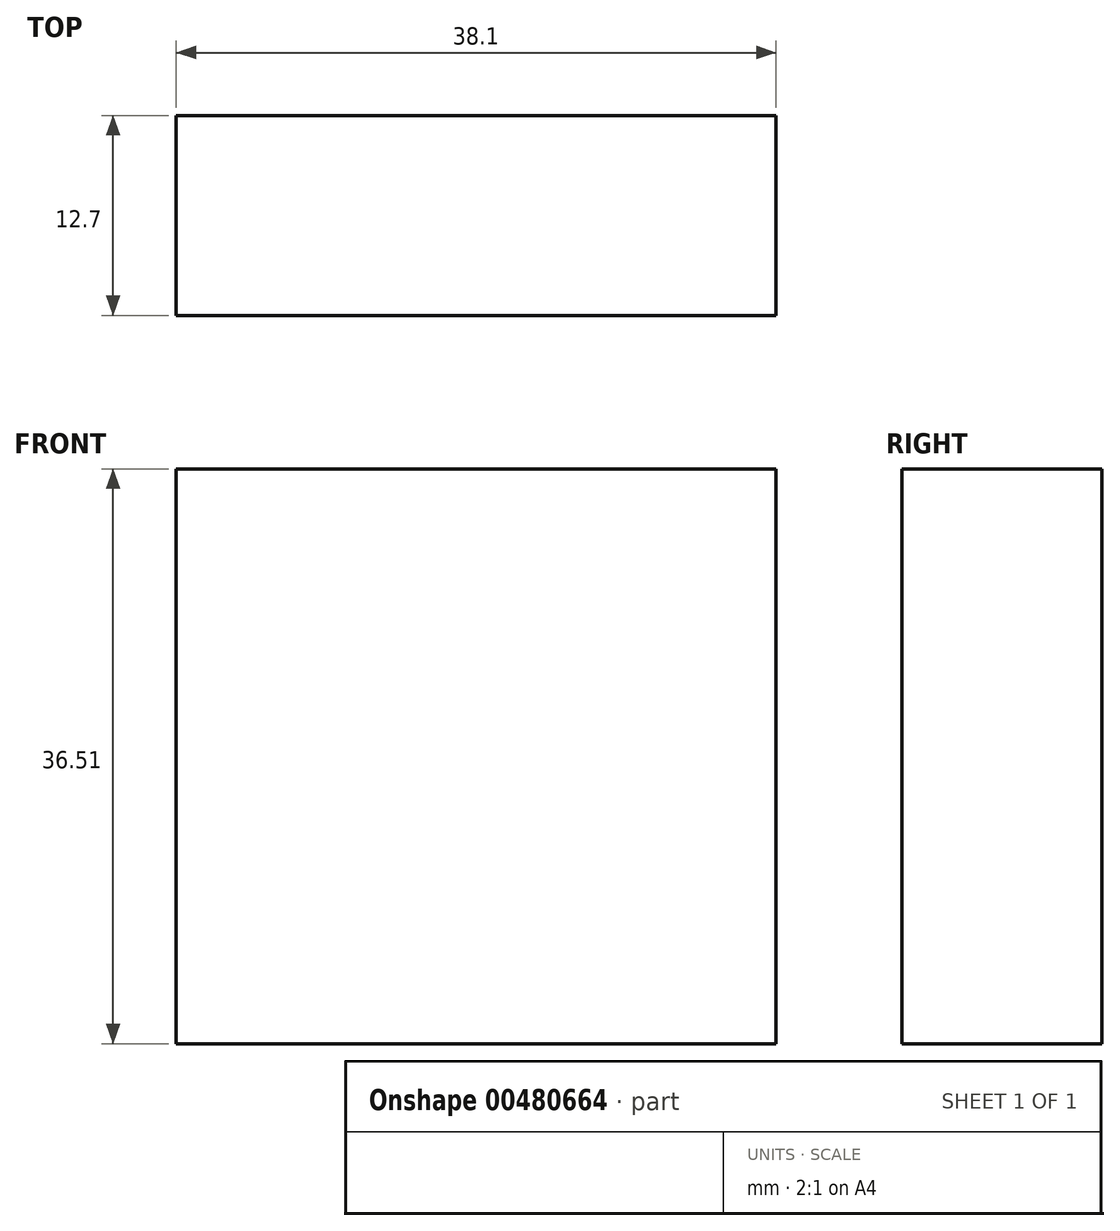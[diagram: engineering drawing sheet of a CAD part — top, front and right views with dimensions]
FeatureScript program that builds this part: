
annotation { "Feature Type Name" : "Feature", "Feature Type Description" : "" }
export const myFeature = defineFeature(function(context is Context, id is Id, definition is map)
    precondition{}
    {
        {
            var Q0;
            Q0=qCreatedBy(makeId("Front.planeOp"),FACE);
            var sketch = newSketch(context, id + "F0", { "sketchPlane" : qUnion([Q0])});
            skLineSegment(sketch, "E0.bottom", {"start": v(-14.39, 26.14) * mm, "end": v(23.71, 26.14) * mm});
            skLineSegment(sketch, "E0.top", {"start": v(-14.39, -10.37) * mm, "end": v(23.71, -10.37) * mm});
            skLineSegment(sketch, "E0.left", {"start": v(-14.39, 26.14) * mm, "end": v(-14.39, -10.37) * mm});
            skLineSegment(sketch, "E0.right", {"start": v(23.71, 26.14) * mm, "end": v(23.71, -10.37) * mm});
            skSolve(sketch);
        }
        {
            var Q0;
            Q0 = qSketchRegion(id + "F0", true);
            extrude(context, id + "F1", {"entities" : qUnion([Q0]), "oppositeDirection" : true, "depth" : 12.7 * mm});
        }
    });
